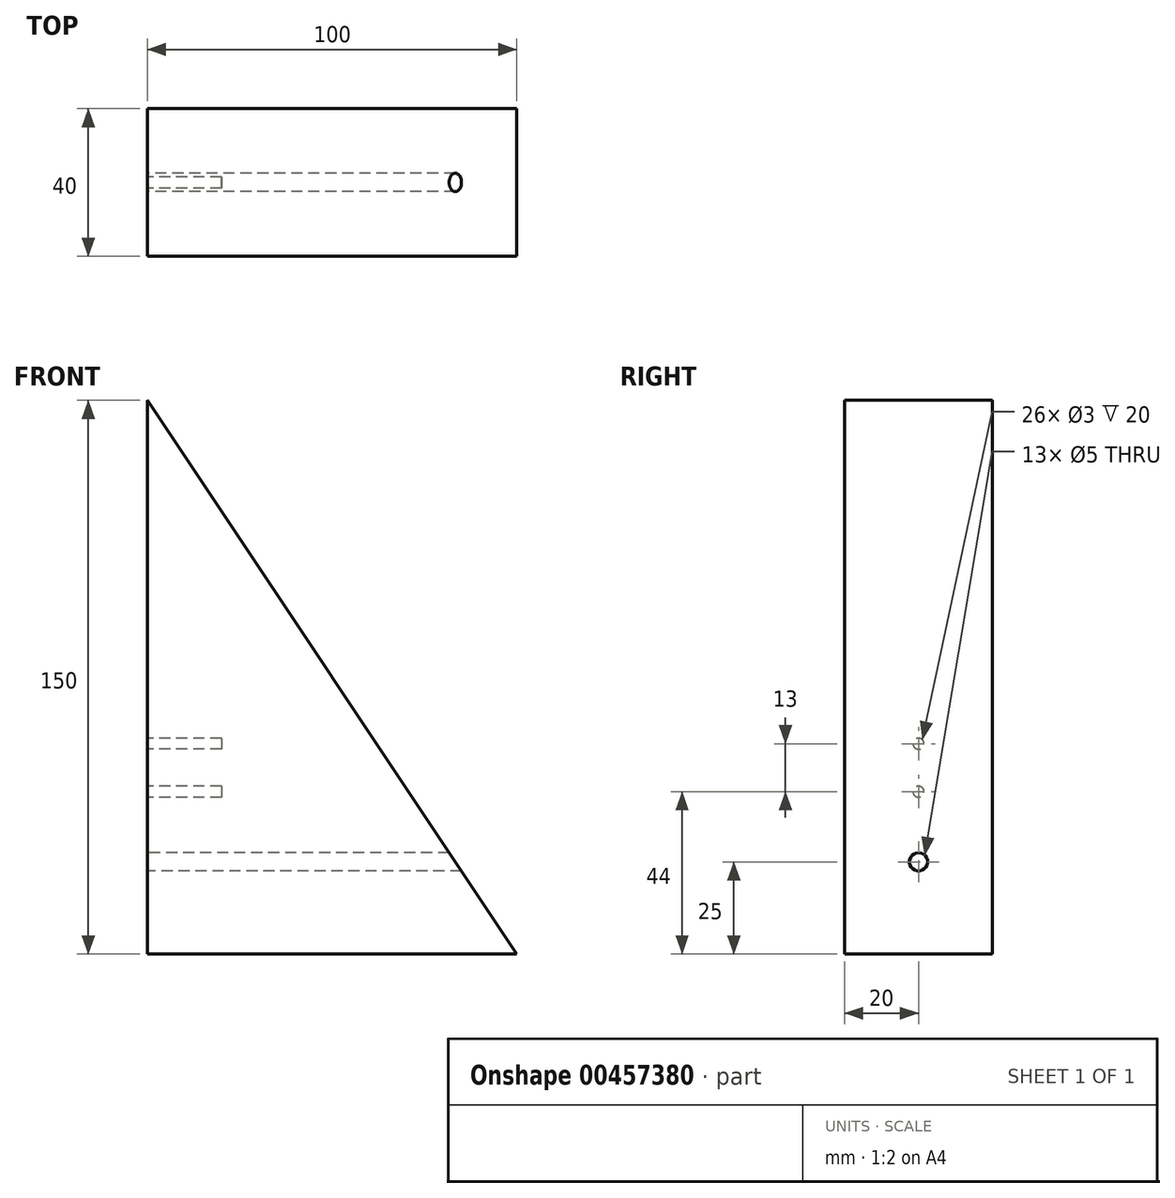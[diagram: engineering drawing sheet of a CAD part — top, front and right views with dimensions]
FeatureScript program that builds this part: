
annotation { "Feature Type Name" : "Feature", "Feature Type Description" : "" }
export const myFeature = defineFeature(function(context is Context, id is Id, definition is map)
    precondition{}
    {
        {
            var Q0;
            Q0=qCreatedBy(makeId("Front.planeOp"),FACE);
            var sketch = newSketch(context, id + "F0", { "sketchPlane" : qUnion([Q0])});
            skLineSegment(sketch, "E0.bottom", {"start": v(0, 0) * mm, "end": v(100, 0) * mm});
            skLineSegment(sketch, "E0.left", {"start": v(0, 0) * mm, "end": v(0, 150) * mm});
            skFitSpline(sketch, "E1", {"points": [v(0, 150) * mm, v(100, 0) * mm], "startDerivative": vector(100, -150) * mm, "endDerivative": vector(100, -150) * mm});
            skSolve(sketch);
        }
        {
            var Q0;
            Q0=makeQuery(id+"F0.imprint","IMPRINT",FACE,{"disambiguationData":[TD([[makeQuery(id+"F0.imprint","IMPRINT",EDGE,{"derivedFrom":sQuery(id+"F0.wireOp",EDGE,"E0.bottom")}),1.0]])]});
            extrude(context, id + "F1", {"entities" : qUnion([Q0]), "depth" : 40 * mm});
        }
        {
            var Q0;
            Q0=makeQuery(id+"F1.opExtrude","SWEPT_FACE",FACE,{"disambiguationData":[OSD([sQuery(id+"F0.wireOp",EDGE,"E0.left")])]});
            var sketch = newSketch(context, id + "F2", { "sketchPlane" : qUnion([Q0])});
            skCircle(sketch, "E2", {"center": v(20, 25) * mm, "radius": 2.5 * mm});
            skPoint(sketch, "E2.centerSnap0", {"position": v(20, 0) * mm});
            skSolve(sketch);
        }
        {
            var Q0;
            Q0=makeQuery(id+"F2.imprint","IMPRINT",FACE,{"disambiguationData":[TD([[makeQuery(id+"F2.imprint","IMPRINT",EDGE,{"derivedFrom":sQuery(id+"F2.wireOp",EDGE,"E2")}),1.0]])]});
            extrude(context, id + "F3", {"entities" : qUnion([Q0]), "operationType" : NewBodyOperationType.REMOVE, "endBound" : BoundingType.THROUGH_ALL, "oppositeDirection" : true, "depth" : 25 * mm});
        }
        {
            var Q0;
            Q0=makeQuery(id+"F1.opExtrude","SWEPT_FACE",FACE,{"disambiguationData":[OSD([sQuery(id+"F0.wireOp",EDGE,"E0.left")])]});
            var sketch = newSketch(context, id + "F4", { "sketchPlane" : qUnion([Q0])});
            skCircle(sketch, "E3", {"center": v(20, 44) * mm, "radius": 1.5 * mm});
            skPoint(sketch, "E3.centerSnap0", {"position": v(20, 0) * mm});
            skCircle(sketch, "E4", {"center": v(20, 57) * mm, "radius": 1.5 * mm});
            skSolve(sketch);
        }
        {
            var Q0;
            Q0=makeQuery(id+"F4.imprint","IMPRINT",FACE,{"disambiguationData":[TD([[makeQuery(id+"F4.imprint","IMPRINT",EDGE,{"derivedFrom":sQuery(id+"F4.wireOp",EDGE,"E4")}),1.0]])]});
            var Q1;
            Q1=makeQuery(id+"F4.imprint","IMPRINT",FACE,{"disambiguationData":[TD([[makeQuery(id+"F4.imprint","IMPRINT",EDGE,{"derivedFrom":sQuery(id+"F4.wireOp",EDGE,"E3")}),1.0]])]});
            extrude(context, id + "F5", {"entities" : qUnion([Q0, Q1]), "operationType" : NewBodyOperationType.REMOVE, "oppositeDirection" : true, "depth" : 20 * mm});
        }
    });
